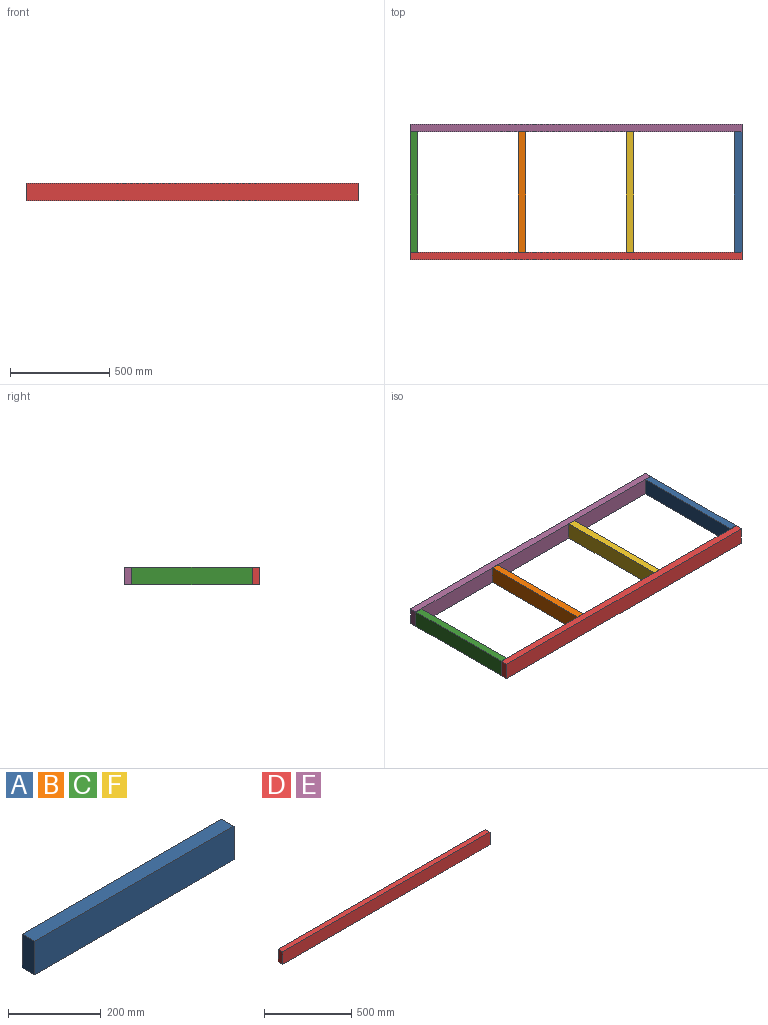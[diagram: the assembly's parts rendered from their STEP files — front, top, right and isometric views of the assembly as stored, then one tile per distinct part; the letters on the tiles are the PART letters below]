
ASSEMBLY  parts=6 mates=5
PART A: 6 faces, bbox 609.6x38.1x88.9 mm
  f0: plane 88.9x38.1mm, normal (-1,0,0), area 3387.1mm2, adj f1,f3,f4,f5
  f1: plane 609.6x38.1mm, normal (0,0,-1), area 23225.8mm2, adj f0,f2,f4,f5
  f2: plane 88.9x38.1mm, normal (1,0,0), area 3387.1mm2, adj f1,f3,f4,f5
  f3: plane 609.6x38.1mm, normal (0,0,1), area 23225.8mm2, adj f0,f2,f4,f5
  f4: plane 609.6x88.9mm, normal (0,-1,0), area 54193.4mm2, adj f0,f1,f2,f3
  f5: plane 609.6x88.9mm, normal (0,1,0), area 54193.4mm2, adj f0,f1,f2,f3
PART B: same geometry as A
PART C: same geometry as A
PART D: 6 faces, bbox 1676.4x38.1x88.9 mm
  f0: plane 88.9x38.1mm, normal (-1,0,0), area 3387.1mm2, adj f1,f3,f4,f5
  f1: plane 1676.4x38.1mm, normal (0,0,-1), area 63870.8mm2, adj f0,f2,f4,f5
  f2: plane 88.9x38.1mm, normal (1,0,0), area 3387.1mm2, adj f1,f3,f4,f5
  f3: plane 1676.4x38.1mm, normal (0,0,1), area 63870.8mm2, adj f0,f2,f4,f5
  f4: plane 1676.4x88.9mm, normal (0,-1,0), area 149032mm2, adj f0,f1,f2,f3
  f5: plane 1676.4x88.9mm, normal (0,1,0), area 149032mm2, adj f0,f1,f2,f3
PART E: same geometry as D
PART F: same geometry as A
PLACE A rot(axis=(0,0,-1),90deg) t=(838.2,285.75,0)mm
PLACE B rot(axis=(0,0,-1),90deg) t=(-254,285.75,0)mm
PLACE C rot(axis=(0,0,1),90deg) t=(-838.2,-323.85,0)mm
PLACE D t=(-838.2,-323.85,0)mm
PLACE E t=(-838.2,323.85,0)mm
PLACE F rot(axis=(0,0,-1),90deg) t=(292.1,285.75,0)mm
MATE fastened D.f5 <-> C.f0  axis (0,1,0) through (-838.2,-323.85,44.45)mm
MATE fastened F.f0 <-> E.f4  axis (0,1,0) through (273.05,285.75,44.45)mm
MATE fastened A.f0 <-> E.f4  axis (0,1,0) through (838.2,285.75,44.45)mm
MATE fastened B.f0 <-> E.f4  axis (0,1,0) through (-273.05,285.75,44.45)mm
MATE fastened C.f2 <-> E.f4  axis (0,1,0) through (-838.2,285.75,44.45)mm
